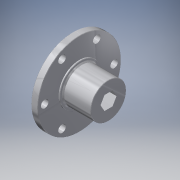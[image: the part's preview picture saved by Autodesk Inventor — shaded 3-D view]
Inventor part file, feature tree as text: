
AUTODESK INVENTOR PART (.ipt)
format: ipt  version: 2016 (Build 200138000, 138)  size: 161,280 bytes
history: native  units: in
note: dims shown in document units (in); Inventor stores cm internally (conversion verified against a paired STEP export)
features: chamfer x1
ambient origin geometry x8: Origin, YZ Plane, XZ Plane, XY Plane, X Axis, Y Axis, Z Axis, Center Point
bodies: Solid1 (feature_tree)
feature tree (1):
  chamfer  "Chamfer4"  [1 undecoded]
note: 1 required parameter value undecoded (feature->parameter linkage not recoverable at this tier; creation-order binding heuristic only, values carry confidence <= 0.55)
